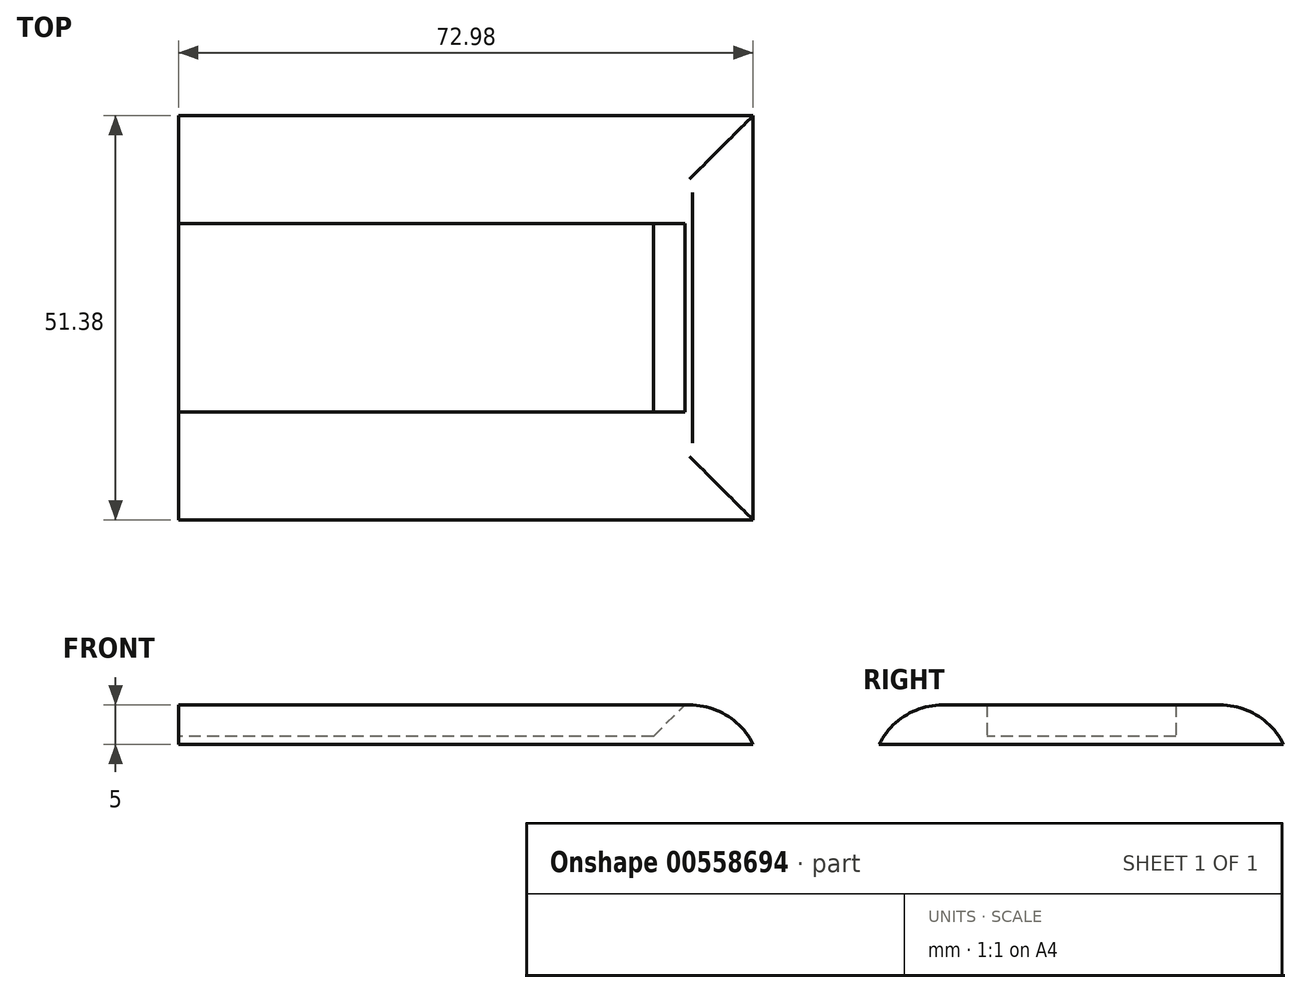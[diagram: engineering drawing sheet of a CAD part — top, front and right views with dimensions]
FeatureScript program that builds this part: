
annotation { "Feature Type Name" : "Feature", "Feature Type Description" : "" }
export const myFeature = defineFeature(function(context is Context, id is Id, definition is map)
    precondition{}
    {
        {
            var Q0;
            Q0=qCreatedBy(makeId("Top.planeOp"),FACE);
            var sketch = newSketch(context, id + "F0", { "sketchPlane" : qUnion([Q0])});
            skLineSegment(sketch, "E0.bottom", {"start": v(28.8, 15.91) * mm, "end": v(-28.8, 15.91) * mm});
            skLineSegment(sketch, "E0.top", {"start": v(28.8, -15.91) * mm, "end": v(-28.8, -15.91) * mm});
            skLineSegment(sketch, "E0.left", {"start": v(28.8, 15.91) * mm, "end": v(28.8, -15.91) * mm});
            skLineSegment(sketch, "E0.right", {"start": v(-28.8, 15.91) * mm, "end": v(-28.8, -15.91) * mm});
            skPoint(sketch, "E0.middle", {"position": v(0, 0) * mm});
            skLineSegment(sketch, "E1.bottom", {"start": v(23.82, 12) * mm, "end": v(-23.82, 12) * mm});
            skLineSegment(sketch, "E1.top", {"start": v(23.82, -12) * mm, "end": v(-23.82, -12) * mm});
            skLineSegment(sketch, "E1.left", {"start": v(23.82, 12) * mm, "end": v(23.82, -12) * mm});
            skLineSegment(sketch, "E1.right", {"start": v(-23.82, 12) * mm, "end": v(-23.82, -12) * mm});
            skLineSegment(sketch, "E2.bottom", {"start": v(-36.49, 25.7) * mm, "end": v(36.49, 25.7) * mm});
            skLineSegment(sketch, "E2.top", {"start": v(-36.49, -25.7) * mm, "end": v(36.49, -25.7) * mm});
            skLineSegment(sketch, "E2.left", {"start": v(-36.49, 25.7) * mm, "end": v(-36.49, -25.7) * mm});
            skLineSegment(sketch, "E2.right", {"start": v(36.49, 25.7) * mm, "end": v(36.49, -25.7) * mm});
            skLineSegment(sketch, "E3", {"start": v(-23.82, 12) * mm, "end": v(-36.49, 12) * mm});
            skLineSegment(sketch, "E4", {"start": v(-23.82, -12) * mm, "end": v(-36.49, -12) * mm});
            skLineSegment(sketch, "E5", {"start": v(-28.8, 15.91) * mm, "end": v(-36.49, 15.91) * mm});
            skLineSegment(sketch, "E6", {"start": v(-28.8, -15.91) * mm, "end": v(-36.49, -15.91) * mm});
            skLineSegment(sketch, "E7.bottom", {"start": v(36.49, -25.7) * mm, "end": v(29.19, -25.7) * mm});
            skLineSegment(sketch, "E7.top", {"start": v(36.49, -32.69) * mm, "end": v(29.19, -32.69) * mm});
            skLineSegment(sketch, "E7.left", {"start": v(36.49, -25.7) * mm, "end": v(36.49, -32.69) * mm});
            skLineSegment(sketch, "E7.right", {"start": v(29.19, -25.7) * mm, "end": v(29.19, -32.69) * mm});
            skLineSegment(sketch, "E8.bottom", {"start": v(36.49, 25.7) * mm, "end": v(29.19, 25.7) * mm});
            skLineSegment(sketch, "E8.top", {"start": v(36.49, 32.69) * mm, "end": v(29.19, 32.69) * mm});
            skLineSegment(sketch, "E8.left", {"start": v(36.49, 25.7) * mm, "end": v(36.49, 32.69) * mm});
            skLineSegment(sketch, "E8.right", {"start": v(29.19, 25.7) * mm, "end": v(29.19, 32.69) * mm});
            skLineSegment(sketch, "E9.bottom", {"start": v(-36.49, -25.7) * mm, "end": v(-29.19, -25.7) * mm});
            skLineSegment(sketch, "E9.top", {"start": v(-36.49, -32.69) * mm, "end": v(-29.19, -32.69) * mm});
            skLineSegment(sketch, "E9.left", {"start": v(-36.49, -25.7) * mm, "end": v(-36.49, -32.69) * mm});
            skLineSegment(sketch, "E9.right", {"start": v(-29.19, -25.7) * mm, "end": v(-29.19, -32.69) * mm});
            skLineSegment(sketch, "E10.bottom", {"start": v(-36.49, 25.7) * mm, "end": v(-29.19, 25.7) * mm});
            skLineSegment(sketch, "E10.top", {"start": v(-36.49, 32.69) * mm, "end": v(-29.19, 32.69) * mm});
            skLineSegment(sketch, "E10.left", {"start": v(-36.49, 25.7) * mm, "end": v(-36.49, 32.69) * mm});
            skLineSegment(sketch, "E10.right", {"start": v(-29.19, 25.7) * mm, "end": v(-29.19, 32.69) * mm});
            skSolve(sketch);
        }
        {
            var Q0;
            Q0=makeQuery(id+"F0.imprint","IMPRINT",FACE,{"disambiguationData":[TD([[makeQuery(id+"F0.imprint","IMPRINT",EDGE,{"derivedFrom":sQuery(id+"F0.wireOp",EDGE,"E0.bottom")}),-1.0]])]});
            extrude(context, id + "F1", {"entities" : qUnion([Q0]), "depth" : 5 * mm, "offsetDistance" : 25 * mm});
        }
        {
            var Q0;
            Q0=makeQuery(id+"F1.opExtrude","CAP_EDGE",EDGE,{"disambiguationData":[OSD([sQuery(id+"F0.wireOp",EDGE,"E2.top")])],"isStart":false});
            var Q1;
            Q1=makeQuery(id+"F1.opExtrude","CAP_EDGE",EDGE,{"disambiguationData":[OSD([sQuery(id+"F0.wireOp",EDGE,"E2.right")])],"isStart":false});
            var Q2;
            Q2=makeQuery(id+"F1.opExtrude","CAP_EDGE",EDGE,{"disambiguationData":[OSD([sQuery(id+"F0.wireOp",EDGE,"E2.bottom")])],"isStart":false});
            fillet(context, id + "F2", {"entities" : qUnion([Q0, Q1, Q2]), "radius" : 9 * mm, "tangentPropagation" : true, "allowEdgeOverflow" : false});
        }
        {
            var Q0;
            {var subQ1=sQuery(id+"F0.wireOp",EDGE,"E0.bottom");Q0=makeQuery(id+"F0.imprint","IMPRINT",FACE,{"disambiguationData":[TD([[makeQuery(id+"F0.imprint","IMPRINT",EDGE,{"derivedFrom":subQ1}),1.0]])]});}
            var Q1;
            {var subQ0=sQuery(id+"F0.wireOp",EDGE,"E5");Q1=makeQuery(id+"F0.imprint","IMPRINT",FACE,{"disambiguationData":[TD([[makeQuery(id+"F0.imprint","IMPRINT",EDGE,{"derivedFrom":subQ0}),1.0]])]});}
            var Q2;
            {var subQ0=sQuery(id+"F0.wireOp",EDGE,"E6");Q2=makeQuery(id+"F0.imprint","IMPRINT",FACE,{"disambiguationData":[TD([[makeQuery(id+"F0.imprint","IMPRINT",EDGE,{"derivedFrom":subQ0}),-1.0]])]});}
            extrude(context, id + "F3", {"entities" : qUnion([Q0, Q1, Q2]), "operationType" : NewBodyOperationType.ADD, "depth" : 5 * mm, "offsetDistance" : 25 * mm});
        }
        {
            var Q0;
            Q0=makeQuery(id+"F3.opExtrude","CAP_EDGE",EDGE,{"disambiguationData":[OSD([sQuery(id+"F0.wireOp",EDGE,"E1.left")])],"isStart":false});
            chamfer(context, id + "F4", {"entities" : qUnion([Q0]), "width" : 4 * mm, "tangentPropagation" : true});
        }
        {
            var Q0;
            Q0=makeQuery(id+"F0.imprint","IMPRINT",FACE,{"disambiguationData":[TD([[makeQuery(id+"F0.imprint","IMPRINT",EDGE,{"derivedFrom":sQuery(id+"F0.wireOp",EDGE,"E1.bottom")}),1.0]])]});
            var Q1;
            {var subQ0=sQuery(id+"F0.wireOp",EDGE,"E3");var subQ1=sQuery(id+"F0.wireOp",EDGE,"E0.right");var subQ2=makeQuery(id+"F0.imprint","INTERSECT",VERTEX,{"derivedFrom":[subQ1,subQ0]});Q1=makeQuery(id+"F0.imprint","IMPRINT",FACE,{"disambiguationData":[TD([[makeQuery(id+"F0.imprint","IMPRINT",EDGE,{"disambiguationData":[TD([[subQ2,-1.0]])],"derivedFrom":subQ1}),-1.0]])]});}
            var Q2;
            {var subQ5=sQuery(id+"F0.wireOp",EDGE,"E1.right");Q2=makeQuery(id+"F0.imprint","IMPRINT",FACE,{"disambiguationData":[TD([[makeQuery(id+"F0.imprint","IMPRINT",EDGE,{"derivedFrom":subQ5}),-1.0]])]});}
            var Q3;
            Q3=makeQuery(id+"F0.imprint","IMPRINT",FACE,{"disambiguationData":[TD([[makeQuery(id+"F0.imprint","IMPRINT",EDGE,{"derivedFrom":sQuery(id+"F0.wireOp",EDGE,"E9.bottom")}),-1.0]])]});
            var Q4;
            Q4=makeQuery(id+"F0.imprint","IMPRINT",FACE,{"disambiguationData":[TD([[makeQuery(id+"F0.imprint","IMPRINT",EDGE,{"derivedFrom":sQuery(id+"F0.wireOp",EDGE,"E7.bottom")}),1.0]])]});
            var Q5;
            Q5=makeQuery(id+"F0.imprint","IMPRINT",FACE,{"disambiguationData":[TD([[makeQuery(id+"F0.imprint","IMPRINT",EDGE,{"derivedFrom":sQuery(id+"F0.wireOp",EDGE,"E10.bottom")}),1.0]])]});
            var Q6;
            Q6=makeQuery(id+"F0.imprint","IMPRINT",FACE,{"disambiguationData":[TD([[makeQuery(id+"F0.imprint","IMPRINT",EDGE,{"derivedFrom":sQuery(id+"F0.wireOp",EDGE,"E8.bottom")}),-1.0]])]});
            extrude(context, id + "F5", {"entities" : qUnion([Q0, Q1, Q2, Q3, Q4, Q5, Q6]), "operationType" : NewBodyOperationType.ADD, "depth" : 1 * mm, "offsetDistance" : 25 * mm});
        }
    });
